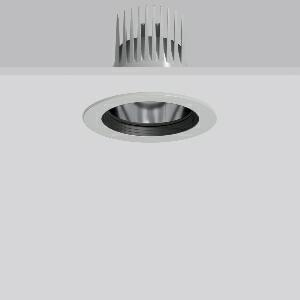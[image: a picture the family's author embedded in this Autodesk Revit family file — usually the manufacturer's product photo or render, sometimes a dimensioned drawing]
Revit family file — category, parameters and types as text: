
# Revit family: heledon_maxi_e_901758_004_07b9
name_source: partatom
category: Lighting Fixtures
units: mm (PartAtom-declared; Revit-internal decimal feet)

## family parameters
Cut with Voids When Loaded = No
Host = Face
Light Source = No
Part Type = Normal
Room Calculation Point = No
Round Connector Dimension = Use Diameter
Shared = No

## types (1)
- HELEDON maxi E (1 x LED Modul 930, 3350 lm, 3000)
    Apparent Load = 25 VA
    Approval mark = CE
    CIE Flux Codes = 100 100 100 100 100
    Color Rendering = 90
    Color Temperature = 3000
    Default Elevation = 1800 mm
    Description = Series: HELEDON maxi
Round recessed downlight. Housing: die-cast aluminium, powder-coated. Black plastic ring and recessed LED to prevent glare from the side. Optical assembly with reflector made of MIRO-Silver with 98% total light reflection for outstanding efficiency - can be changed without tools. Best colour rendering index Ra>90. Suitable for Recessed ceiling mounting. Installation without tools thanks to spring fastening system. Including separate LED converter with connecting cable 600 mm.High quality converter without flickering and stroboscopic effect. Through-wiring box (5 pole) available as accessory. The following accessories can be mounted without use of tools: interchangeable lenses, decorative glasses, honeycomb louvre, clear and frosted diffusers, white interchangeable plastic ring. 
Colour: silver
Diameter: 162 mm
Height: 3 mm
Cut-out diameter: 152 mm
Recess height: 200 mm
Luminaire: recess height: 135 mm
Lamp: LED
Socket: without socket
Colour temperature: 3000K
Colour rendering index (CRI): 92
System power: 25 W
Rated luminous flux: 3350 lm
Luminous efficiency: 134 lm/W
Control gear: Regulated power supply
Protection class: II
Type of protection: IP 20
    Height = 0 mm  [stored 0 ft]
    Lamp = 1 x LED Modul 930
    Lamp Light Flux = 3350 lm
    Lamp count = 1
    Length = 162 mm
    Lifetime = 50000 h
    Luminous efficacy = 134 lm/W
    Manufacturer = RZB
    ModVariant = No
    Model = 901758.004
    Mounting Place = Ceiling
    Mounting Type = Recessed
    Number of Poles = 1
    OnlyDefault = Yes
    Power Factor = 1
    Product Name = HELEDON maxi E
    Product group = Recessed downlights
    ProductGroupID = 402
    Protection Class = Protection class II
    Protection Degree = IP 20
    RLX_Detail_Level = 1
    RLX_Emergency_Light_Flux = 0 lm
    RLX_Emergency_Type = 0
    RLX_Emergency_Type_DB = No
    RlxData = <blob elided: 118793 chars, md5=3df1d9ee>
    Socket = socket
    Standby Power = 0 W
    System Light Flux = 3350 lm
    System Power = 25 W
    Type Comments = Product without accessories
    Type Image = 901662.004.jpg
    URL = http://relux.com
    VarID = ---
    Voltage = 230 V
    Voltage Range = 220-240 V
    Weight = 0.00 kg
    Width = 0 mm  [stored 0 ft]

note: [stored X ft] marks values corroborated as IEEE doubles in the binary element streams (Revit-internal decimal feet)

## geometry (parser evidence)
native form markers: Blend x4, Sweep x11
no freeform markers — native parametric forms only
